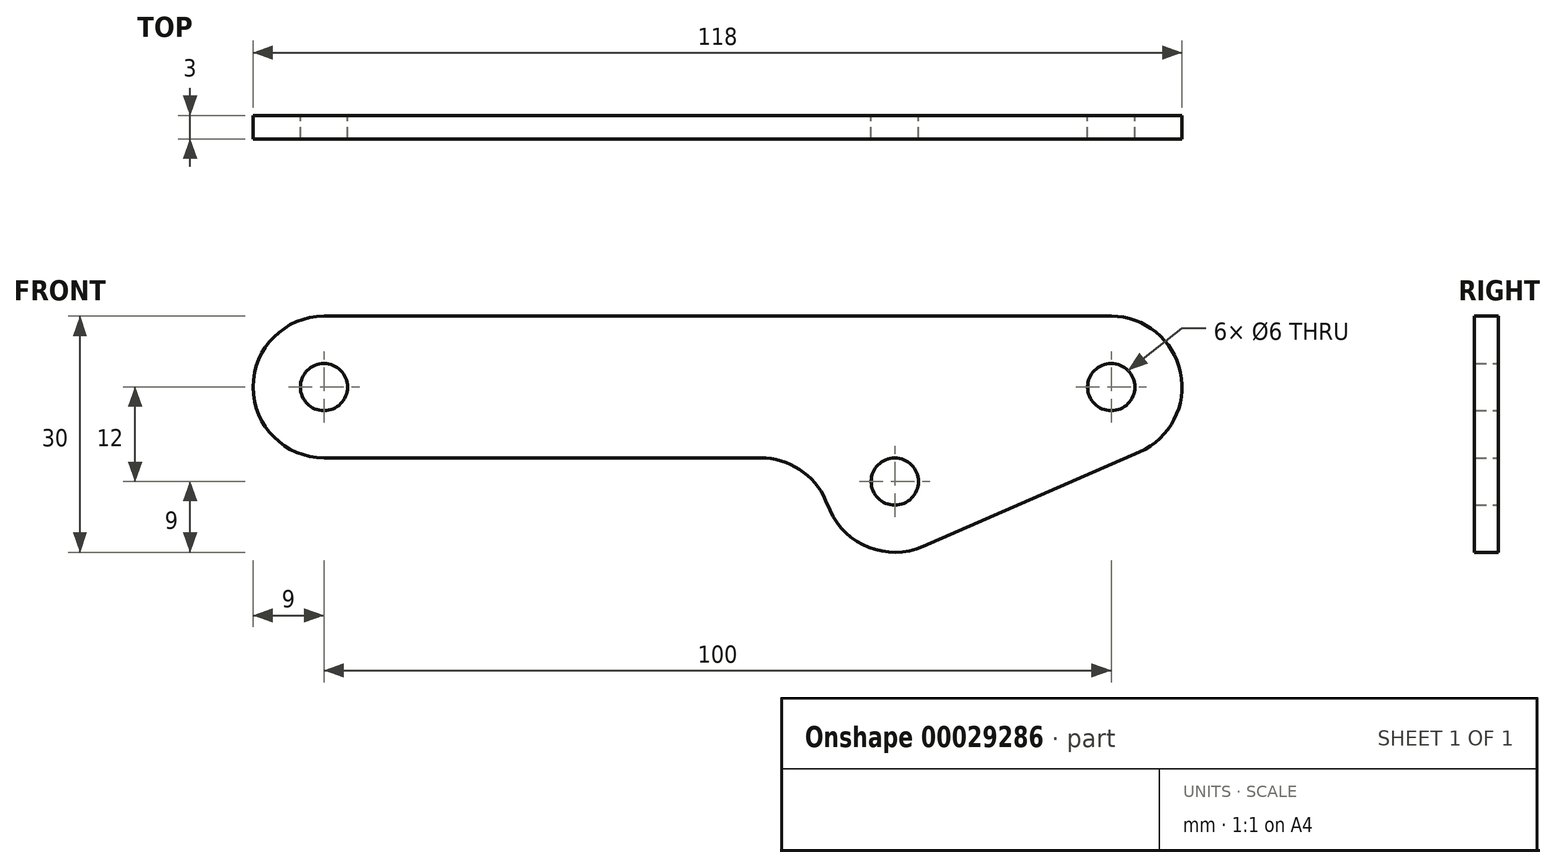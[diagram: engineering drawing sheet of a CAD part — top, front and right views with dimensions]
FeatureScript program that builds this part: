
annotation { "Feature Type Name" : "Feature", "Feature Type Description" : "" }
export const myFeature = defineFeature(function(context is Context, id is Id, definition is map)
    precondition{}
    {
        {
            var Q0;
            Q0=qCreatedBy(makeId("Front.planeOp"),FACE);
            var sketch = newSketch(context, id + "F0", { "sketchPlane" : qUnion([Q0])});
            skLineSegment(sketch, "E0", {"start": v(9, 0) * mm, "end": v(64.48, 0) * mm});
            skLineSegment(sketch, "E1", {"start": v(72.73, -5.4) * mm, "end": v(73.26, -6.6) * mm});
            skLineSegment(sketch, "E2", {"start": v(85.1, -11.25) * mm, "end": v(112.6, 0.75) * mm});
            skLineSegment(sketch, "E3", {"start": v(117.25, 12.6) * mm, "end": v(117.25, 12.6) * mm});
            skLineSegment(sketch, "E4", {"start": v(109, 18) * mm, "end": v(9, 18) * mm});
            skLineSegment(sketch, "E5", {"start": v(0, 9) * mm, "end": v(0, 9) * mm});
            skCircle(sketch, "E6", {"center": v(81.5, -3) * mm, "radius": 3 * mm});
            skCircle(sketch, "E7", {"center": v(109, 9) * mm, "radius": 3 * mm});
            skCircle(sketch, "E8", {"center": v(9, 9) * mm, "radius": 3 * mm});
            skPoint(sketch, "E9.visualSharp", {"position": v(0, 18) * mm});
            skArc(sketch, "E9.filletArc", {"start": v(9, 18) * mm, "mid": v(2.64, 15.36) * mm, "end": v(0, 9) * mm});
            skPoint(sketch, "E10.visualSharp", {"position": v(113.65, 20.85) * mm});
            skArc(sketch, "E10.filletArc", {"start": v(117.25, 12.6) * mm, "mid": v(113.93, 16.53) * mm, "end": v(109, 18) * mm});
            skPoint(sketch, "E11.visualSharp", {"position": v(120.85, 4.35) * mm});
            skArc(sketch, "E11.filletArc", {"start": v(112.6, 0.75) * mm, "mid": v(117.38, 5.71) * mm, "end": v(117.25, 12.6) * mm});
            skPoint(sketch, "E12.visualSharp", {"position": v(76.86, -14.85) * mm});
            skArc(sketch, "E12.filletArc", {"start": v(73.26, -6.6) * mm, "mid": v(78.22, -11.38) * mm, "end": v(85.1, -11.25) * mm});
            skPoint(sketch, "E13.visualSharp", {"position": v(70.38, 0) * mm});
            skArc(sketch, "E13.filletArc", {"start": v(72.73, -5.4) * mm, "mid": v(69.41, -1.47) * mm, "end": v(64.48, 0) * mm});
            skPoint(sketch, "E14.visualSharp", {"position": v(0, 0) * mm});
            skArc(sketch, "E14.filletArc", {"start": v(0, 9) * mm, "mid": v(2.64, 2.64) * mm, "end": v(9, 0) * mm});
            skSolve(sketch);
        }
        {
            var Q0;
            Q0 = qSketchRegion(id + "F0", true);
            extrude(context, id + "F1", {"entities" : qUnion([Q0]), "depth" : 3 * mm});
        }
    });
